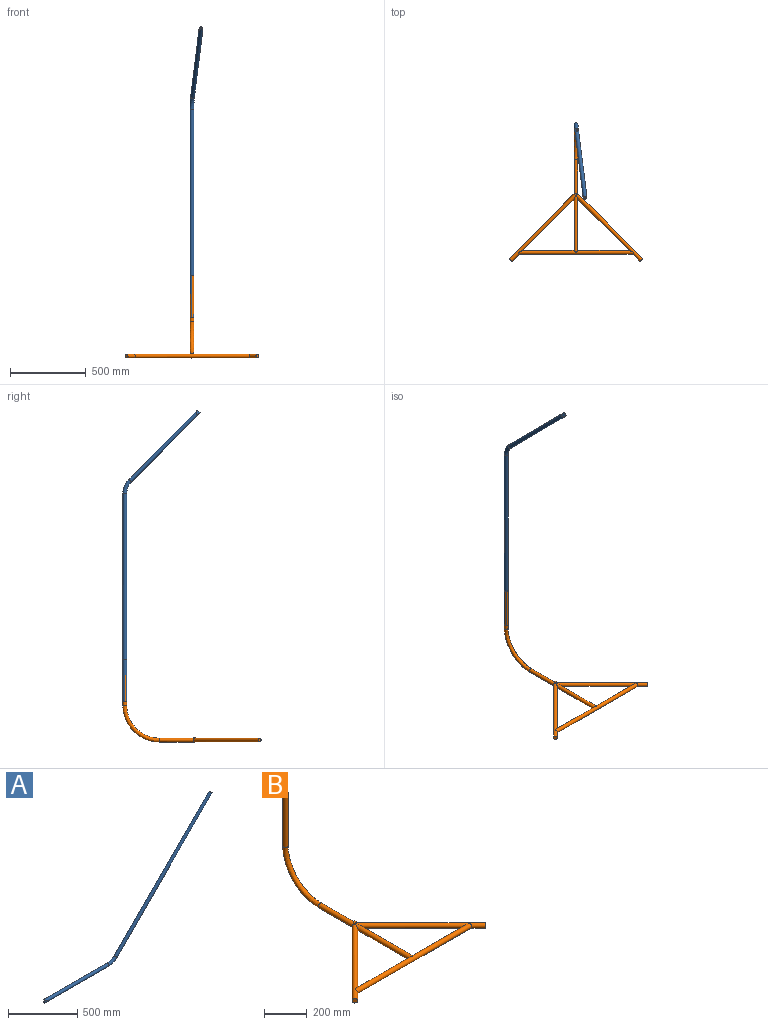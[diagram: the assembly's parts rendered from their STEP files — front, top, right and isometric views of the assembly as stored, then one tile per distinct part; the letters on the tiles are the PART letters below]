
ASSEMBLY  parts=2 mates=1
PART A: 12 faces, bbox 1707.4x25.4x1035.5 mm
  f0: cylinder r=12.7mm len=647.7mm, axis (1,0,0), area 50424.4mm2, adj f1,f3,f6,f7,f8,f10,f11
  f1: plane 25.4x6.38mm, normal (-1,0,0), area 160.3mm2, adj f0,f10,f11
  f2: plane 25.4x17.96mm, normal (0.71,0,0.71), area 506.7mm2, adj f4
  f3: torus R=114.3mm, axis (0,-1,0), area 7163.4mm2, adj f0,f4,f5
  f4: cylinder r=12.7mm len=987.83mm, axis (0.71,0,0.71), area 109448.8mm2, adj f2,f3
  f5: plane 6.35x2.54mm, normal (-1,0,0), area 15.3mm2, adj f3,f6,f8,f9
  f6: plane 25.4x2.14mm, normal (0,-1,0), area 54.3mm2, adj f0,f5,f7,f9
  f7: plane 6.35x2.54mm, normal (1,0,0), area 15.3mm2, adj f0,f6,f8,f9
  f8: plane 25.4x2.14mm, normal (0,1,0), area 54.3mm2, adj f0,f5,f7,f9
  f9: plane 25.4x6.35mm, normal (0,0,-1), area 161.3mm2, adj f5,f6,f7,f8
  f10: plane 25.35x24.58mm, normal (-0.35,-0.94,0), area 492.7mm2, adj f0,f1
  f11: plane 25.4x24.59mm, normal (-0.35,0.94,0), area 494.3mm2, adj f0,f1
PART B: 25 faces, bbox 879.3x911x544 mm
  f0: cylinder r=12.7mm len=230.38mm, axis (0,1,0), area 17962.1mm2, adj f2,f3,f8,f10,f18,f19,f20,f24
  f1: cylinder r=12.7mm len=379.22mm, axis (0,1,0), area 28156.3mm2, adj f2,f3,f4,f6,f10,f16,f22
  f2: cylinder r=12.7mm len=449.01mm, axis (-0.71,0.71,0), area 46783.1mm2, adj f0,f1,f9,f10,f12,f15,f16,f17
  f3: cylinder r=12.7mm len=448.12mm, axis (0.71,0.71,0), area 46683.4mm2, adj f0,f1,f11,f13,f14,f16,f20,f21
  f4: plane 1.09x0.01mm, normal (0,-1,0), area 0mm2, adj f1,f16
  f5: plane 25.4x25.4mm, normal (0,0,1), area 506.7mm2, adj f7
  f6: plane 1.09x0.01mm, normal (0,-1,0), area 0mm2, adj f1,f16
  f7: cylinder r=12.7mm len=304.86mm, axis (0,0,1), area 24323.2mm2, adj f5,f8
  f8: bspline ~241.29x239.38mm, area 28466.9mm2, adj f0,f7
  f9: plane 25.4x17.96mm, normal (0.71,-0.71,0), area 506.7mm2, adj f2
  f10: cylinder r=12.7mm len=1.82mm, axis (0.71,0.71,0), area 0.9mm2, adj f0,f1,f2
  f11: plane 25.4x17.96mm, normal (-0.71,-0.71,0), area 506.7mm2, adj f3
  f12: plane 4.3x0.55mm, normal (1,0,0), area 0.3mm2, adj f2,f16
  f13: plane 3.03x0.28mm, normal (-1,0,0), area 0.1mm2, adj f3,f16
  f14: plane 3.03x0.28mm, normal (-1,0,0), area 0.1mm2, adj f3,f16
  f15: plane 4.31x0.57mm, normal (1,0,0), area 0.3mm2, adj f2,f16
  f16: cylinder r=12.7mm len=758.79mm, axis (1,0,0), area 58275.9mm2, adj f1,f2,f3,f4,f6,f12,f13,f14
  f17: plane 8.22x6.89mm, normal (0.83,-0.55,0), area 60mm2, adj f2,f18,f22,f23
  f18: plane 8.87x7.44mm, normal (0.9,0.44,0), area 69.1mm2, adj f0,f2,f17,f19,f23
  f19: plane 8.23x7.84mm, normal (0.06,1,0), area 59.5mm2, adj f0,f18,f20,f23
  f20: plane 9.53x6.86mm, normal (-0.83,0.55,0), area 70.2mm2, adj f0,f3,f19,f21,f23,f24
  f21: plane 9.54x7.53mm, normal (-0.9,-0.44,0), area 63.6mm2, adj f3,f20,f22,f23
  f22: plane 8.23x7.37mm, normal (-0.06,-1,0), area 58.5mm2, adj f1,f2,f3,f17,f21,f23
  f23: plane 16.45x14.78mm, normal (0,0,1), area 176.5mm2, adj f17,f18,f19,f20,f21,f22
  f24: plane 0.19x0.13mm, normal (0,0,-1), area 0mm2, adj f0,f3,f20
PLACE A rot(axis=(0.64,0.72,-0.26),146.7deg) t=(-43.27,495.44,1618.19)mm
PLACE B t=(-47.43,300.07,-89.62)mm fixed
MATE cylindrical B.f7 <-> A.f4  axis (0,0,1) through (-47.43,528.66,441.54)mm
